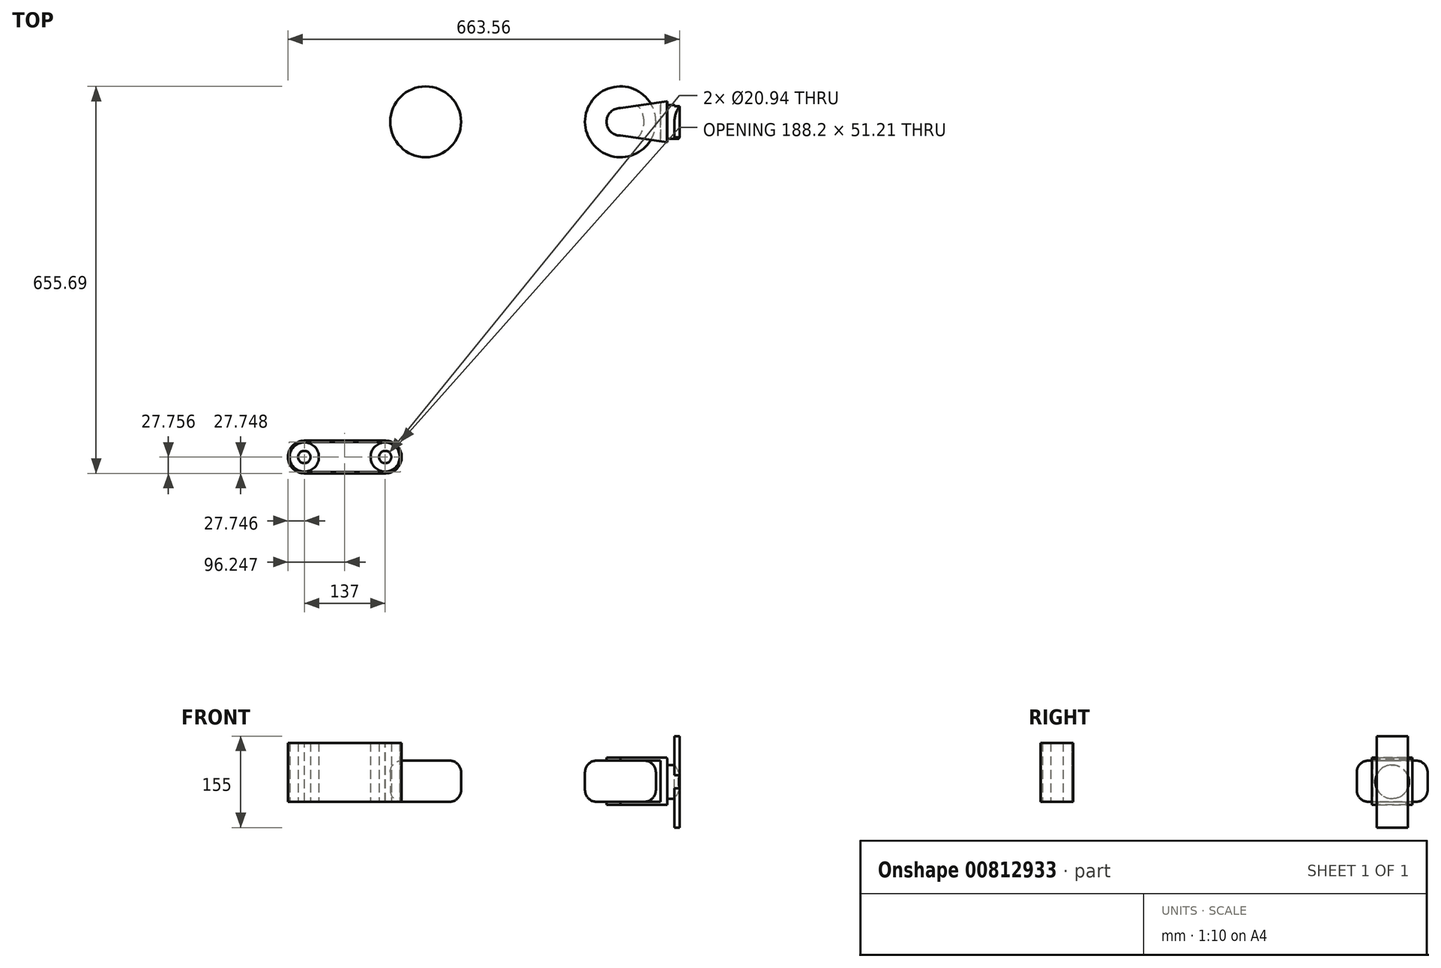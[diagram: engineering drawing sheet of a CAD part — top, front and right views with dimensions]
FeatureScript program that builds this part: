
annotation { "Feature Type Name" : "Feature", "Feature Type Description" : "" }
export const myFeature = defineFeature(function(context is Context, id is Id, definition is map)
    precondition{}
    {
        {
            var Q0;
            Q0=qCreatedBy(makeId("Top.planeOp"),FACE);
            var sketch = newSketch(context, id + "F0", { "sketchPlane" : qUnion([Q0])});
            skCircle(sketch, "E0", {"center": v(-28.53, 29.73) * mm, "radius": 6 * mm});
            skSolve(sketch);
        }
        {
            var Q0;
            Q0=makeQuery(id+"F0.imprint","IMPRINT",FACE,{"disambiguationData":[TD([[makeQuery(id+"F0.imprint","IMPRINT",EDGE,{"derivedFrom":sQuery(id+"F0.wireOp",EDGE,"E0")}),1.0]])]});
            var Q1;
            Q1=sQuery(id+"F0.wireOp",EDGE,"E0");
            extrude(context, id + "F1", {"entities" : qUnion([Q0]), "surfaceEntities" : qUnion([Q1]), "depth" : 7 * mm, "offsetDistance" : 25 * mm});
        }
        {
            var Q0;
            Q0=makeQuery(id+"F1.opExtrude","CAP_EDGE",EDGE,{"disambiguationData":[OSD([sQuery(id+"F0.wireOp",EDGE,"E0")])],"isStart":false});
            var Q1;
            Q1=makeQuery(id+"F1.opExtrude","CAP_EDGE",EDGE,{"disambiguationData":[OSD([sQuery(id+"F0.wireOp",EDGE,"E0")])],"isStart":true});
            fillet(context, id + "F2", {"entities" : qUnion([Q0, Q1]), "radius" : 2 * mm, "tangentPropagation" : true, "allowEdgeOverflow" : false});
        }
        {
            var Q0;
            Q0=makeQuery(id+"F1.opExtrude","SWEPT_BODY",BODY,{"disambiguationData":[OSD([sQuery(id+"F0.wireOp",EDGE,"E0")])]});
            transform(context, id + "F3", {"entities" : qUnion([Q0]), "transformType" : TransformType.TRANSLATION_3D, "dx" : 0 * mm, "dy" : 0 * mm, "dz" : 0 * mm, "makeCopy" : true});
        }
        {
            var Q0;
            Q0=makeQuery(id+"F3.opPattern","COPY",BODY,{"derivedFrom":makeQuery(id+"F1.opExtrude","SWEPT_BODY",BODY,{"disambiguationData":[OSD([sQuery(id+"F0.wireOp",EDGE,"E0")])]}),"instanceName":"1"});
            transform(context, id + "F4", {"entities" : qUnion([Q0]), "transformType" : TransformType.TRANSLATION_3D, "dx" : 33 * mm, "dy" : 0 * mm, "dz" : 0 * mm, "makeCopy" : false});
        }
        {
            var Q0;
            Q0=makeQuery(id+"F3.opPattern","COPY",FACE,{"derivedFrom":makeQuery(id+"F1.opExtrude","CAP_FACE",FACE,{"disambiguationData":[OSD([sQuery(id+"F0.wireOp",EDGE,"E0")])],"isStart":true}),"instanceName":"1"});
            var sketch = newSketch(context, id + "F5", { "sketchPlane" : qUnion([Q0])});
            skCircle(sketch, "E1", {"center": v(4.47, -29.73) * mm, "radius": 2.33 * mm});
            skLineSegment(sketch, "E2", {"start": v(4.47, -27.4) * mm, "end": v(12.39, -26.29) * mm});
            skLineSegment(sketch, "E3", {"start": v(4.47, -32.06) * mm, "end": v(12.39, -33.18) * mm});
            skLineSegment(sketch, "E4", {"start": v(12.39, -33.18) * mm, "end": v(12.39, -26.29) * mm});
            skSolve(sketch);
        }
        {
            var Q0;
            {var subQ0=sQuery(id+"F5.wireOp",EDGE,"E1");var subQ1=makeQuery(id+"F5.imprint","INTERSECT",VERTEX,{"derivedFrom":[subQ0,sQuery(id+"F5.wireOp",EDGE,"E2")]});Q0=makeQuery(id+"F5.imprint","IMPRINT",FACE,{"disambiguationData":[TD([[makeQuery(id+"F5.imprint","IMPRINT",EDGE,{"disambiguationData":[TD([[subQ1,-1.0]])],"derivedFrom":subQ0}),1.0]])]});}
            var Q1;
            {var subQ0=sQuery(id+"F5.wireOp",EDGE,"E2");var subQ1=sQuery(id+"F5.wireOp",EDGE,"E1");var subQ2=makeQuery(id+"F5.imprint","INTERSECT",VERTEX,{"derivedFrom":[subQ1,subQ0]});Q1=makeQuery(id+"F5.imprint","IMPRINT",FACE,{"disambiguationData":[TD([[makeQuery(id+"F5.imprint","IMPRINT",EDGE,{"disambiguationData":[TD([[subQ2,1.0]])],"derivedFrom":subQ1}),-1.0]])]});}
            var Q2;
            {var subQ0=sQuery(id+"F5.wireOp",EDGE,"E4");Q2=makeQuery(id+"F5.imprint","IMPRINT",FACE,{"disambiguationData":[TD([[makeQuery(id+"F5.imprint","IMPRINT",EDGE,{"derivedFrom":subQ0}),1.0]])]});}
            extrude(context, id + "F6", {"entities" : qUnion([Q0, Q1, Q2]), "operationType" : NewBodyOperationType.ADD, "depth" : 0.5 * mm, "offsetDistance" : 25 * mm});
        }
        {
            var Q0;
            Q0=makeQuery(id+"F3.opPattern","COPY",FACE,{"derivedFrom":makeQuery(id+"F1.opExtrude","CAP_FACE",FACE,{"disambiguationData":[OSD([sQuery(id+"F0.wireOp",EDGE,"E0")])],"isStart":false}),"instanceName":"1"});
            var sketch = newSketch(context, id + "F7", { "sketchPlane" : qUnion([Q0])});
            skCircle(sketch, "E5", {"center": v(4.44, 29.73) * mm, "radius": 2.33 * mm});
            skLineSegment(sketch, "E6", {"start": v(4.44, 32.06) * mm, "end": v(12.36, 33.18) * mm});
            skLineSegment(sketch, "E7", {"start": v(4.44, 27.4) * mm, "end": v(12.36, 26.29) * mm});
            skLineSegment(sketch, "E8", {"start": v(12.36, 26.29) * mm, "end": v(12.36, 33.18) * mm});
            skSolve(sketch);
        }
        {
            var Q0;
            Q0 = qSketchRegion(id + "F7", true);
            extrude(context, id + "F8", {"entities" : qUnion([Q0]), "operationType" : NewBodyOperationType.ADD, "depth" : 0.5 * mm, "offsetDistance" : 25 * mm});
        }
        {
            var Q0;
            Q0=makeQuery(id+"F6.opExtrude","CAP_FACE",FACE,{"disambiguationData":[OSD([sQuery(id+"F5.wireOp",EDGE,"E1"),sQuery(id+"F5.wireOp",EDGE,"E2"),sQuery(id+"F5.wireOp",EDGE,"E3"),sQuery(id+"F5.wireOp",EDGE,"E4")])],"isStart":true});
            var sketch = newSketch(context, id + "F9", { "sketchPlane" : qUnion([Q0])});
            skLineSegment(sketch, "E9", {"start": v(11.26, 33.02) * mm, "end": v(12.39, 33.18) * mm});
            skLineSegment(sketch, "E10", {"start": v(12.39, 33.18) * mm, "end": v(12.39, 26.29) * mm});
            skLineSegment(sketch, "E11", {"start": v(12.39, 26.29) * mm, "end": v(11.26, 26.44) * mm});
            skLineSegment(sketch, "E12", {"start": v(11.26, 26.44) * mm, "end": v(11.26, 33.02) * mm});
            skSolve(sketch);
        }
        {
            var Q0;
            Q0 = qSketchRegion(id + "F9", true);
            extrude(context, id + "F10", {"entities" : qUnion([Q0]), "operationType" : NewBodyOperationType.ADD, "depth" : 7.3 * mm, "offsetDistance" : 25 * mm});
        }
        {
            var Q0;
            Q0=makeQuery(id+"F10.boolean.opBoolean","MERGE",FACE,{"derivedFrom":[makeQuery(id+"F6.opExtrude","SWEPT_FACE",FACE,{"disambiguationData":[OSD([sQuery(id+"F5.wireOp",EDGE,"E4")])]}),makeQuery(id+"F10.opExtrude","SWEPT_FACE",FACE,{"disambiguationData":[OSD([sQuery(id+"F9.wireOp",EDGE,"E10")])]})]});
            var sketch = newSketch(context, id + "F11", { "sketchPlane" : qUnion([Q0])});
            skCircle(sketch, "E13", {"center": v(29.73, 3.4) * mm, "radius": 2.86 * mm});
            skPoint(sketch, "E13.centerSnap0", {"position": v(26.29, 3.4) * mm});
            skPoint(sketch, "E13.centerSnap1", {"position": v(29.73, 7.3) * mm});
            skSolve(sketch);
        }
        {
            var Q0;
            Q0 = qSketchRegion(id + "F11", true);
            extrude(context, id + "F12", {"entities" : qUnion([Q0]), "operationType" : NewBodyOperationType.ADD, "depth" : 1.2 * mm, "offsetDistance" : 25 * mm});
        }
        {
            var Q0;
            Q0=makeQuery(id+"F12.opExtrude","CAP_FACE",FACE,{"disambiguationData":[OSD([sQuery(id+"F11.wireOp",EDGE,"E13")])],"isStart":false});
            var sketch = newSketch(context, id + "F13", { "sketchPlane" : qUnion([Q0])});
            skLineSegment(sketch, "E14.bottom", {"start": v(32.37, -4.35) * mm, "end": v(27.1, -4.35) * mm});
            skLineSegment(sketch, "E14.top", {"start": v(32.37, 11.15) * mm, "end": v(27.1, 11.15) * mm});
            skLineSegment(sketch, "E14.left", {"start": v(32.37, -4.35) * mm, "end": v(32.37, 11.15) * mm});
            skLineSegment(sketch, "E14.right", {"start": v(27.1, -4.35) * mm, "end": v(27.1, 11.15) * mm});
            skPoint(sketch, "E14.middle", {"position": v(29.73, 3.4) * mm});
            skSolve(sketch);
        }
        {
            var Q0;
            {var subQ0=sQuery(id+"F13.wireOp",EDGE,"E14.top");Q0=makeQuery(id+"F13.imprint","IMPRINT",FACE,{"disambiguationData":[TD([[makeQuery(id+"F13.imprint","IMPRINT",EDGE,{"derivedFrom":subQ0}),1.0]])]});}
            var Q1;
            {var subQ0=sQuery(id+"F13.wireOp",EDGE,"E14.bottom");Q1=makeQuery(id+"F13.imprint","IMPRINT",FACE,{"disambiguationData":[TD([[makeQuery(id+"F13.imprint","IMPRINT",EDGE,{"derivedFrom":subQ0}),-1.0]])]});}
            var Q2;
            {var subQ0=sQuery(id+"F13.wireOp",EDGE,"E14.left");var subQ1=makeQuery(id+"F12.opExtrude","CAP_EDGE",EDGE,{"disambiguationData":[OSD([sQuery(id+"F11.wireOp",EDGE,"E13")])],"isStart":false});var subQ2=makeQuery(id+"F13.imprint","INTERSECT",VERTEX,{"disambiguationData":[OD(0.0)],"derivedFrom":[subQ1,subQ0]});Q2=makeQuery(id+"F13.imprint","IMPRINT",FACE,{"disambiguationData":[TD([[makeQuery(id+"F13.imprint","IMPRINT",EDGE,{"disambiguationData":[TD([[subQ2,-1.0]])],"derivedFrom":subQ0}),1.0]])]});}
            extrude(context, id + "F14", {"entities" : qUnion([Q0, Q1, Q2]), "operationType" : NewBodyOperationType.ADD, "depth" : 0.9 * mm, "offsetDistance" : 25 * mm});
        }
        {
            var Q0;
            {var subQ0=sQuery(id+"F13.wireOp",EDGE,"E14.left");Q0=makeQuery(id+"F14.boolean.opBoolean","SPLIT",EDGE,{"disambiguationData":[topologyDisambiguationEdgeConnected([makeQuery(id+"F12.opExtrude","CAP_FACE",FACE,{"disambiguationData":[OSD([sQuery(id+"F11.wireOp",EDGE,"E13")])],"isStart":false}),makeQuery(id+"F14.opExtrude","SWEPT_FACE",FACE,{"disambiguationData":[OSD([subQ0])]})])],"derivedFrom":makeQuery(id+"F14.opExtrude","CAP_EDGE",EDGE,{"disambiguationData":[OSD([subQ0])],"isStart":true})});}
            fillet(context, id + "F15", {"entities" : qUnion([Q0]), "radius" : 5 * mm, "tangentPropagation" : true, "allowEdgeOverflow" : false});
        }
        {
            var Q0;
            {var subQ0=sQuery(id+"F13.wireOp",EDGE,"E14.right");Q0=makeQuery(id+"F14.boolean.opBoolean","SPLIT",EDGE,{"disambiguationData":[topologyDisambiguationEdgeConnected([makeQuery(id+"F12.opExtrude","CAP_FACE",FACE,{"disambiguationData":[OSD([sQuery(id+"F11.wireOp",EDGE,"E13")])],"isStart":false}),makeQuery(id+"F14.opExtrude","SWEPT_FACE",FACE,{"disambiguationData":[OSD([subQ0])]})])],"derivedFrom":makeQuery(id+"F14.opExtrude","CAP_EDGE",EDGE,{"disambiguationData":[OSD([subQ0])],"isStart":true})});}
            fillet(context, id + "F16", {"entities" : qUnion([Q0]), "radius" : 5 * mm, "tangentPropagation" : true, "allowEdgeOverflow" : false});
        }
        {
            var Q0;
            Q0=qCreatedBy(makeId("Top.planeOp"),FACE);
            var sketch = newSketch(context, id + "F17", { "sketchPlane" : qUnion([Q0])});
            skCircle(sketch, "E15", {"center": v(-49.1, -27.06) * mm, "radius": 2.47 * mm});
            skCircle(sketch, "E16", {"center": v(-49.1, -27.06) * mm, "radius": 1.05 * mm});
            skSolve(sketch);
        }
        {
            var Q0;
            Q0=makeQuery(id+"F17.imprint","IMPRINT",FACE,{"disambiguationData":[TD([[makeQuery(id+"F17.imprint","IMPRINT",EDGE,{"derivedFrom":sQuery(id+"F17.wireOp",EDGE,"E15")}),1.0]])]});
            extrude(context, id + "F18", {"entities" : qUnion([Q0]), "depth" : 10 * mm, "offsetDistance" : 25 * mm});
        }
        {
            var Q0;
            Q0=makeQuery(id+"F18.opExtrude","SWEPT_BODY",BODY,{"disambiguationData":[OSD([sQuery(id+"F17.wireOp",EDGE,"E15"),sQuery(id+"F17.wireOp",EDGE,"E16")])]});
            transform(context, id + "F19", {"entities" : qUnion([Q0]), "transformType" : TransformType.TRANSLATION_3D, "dx" : 13.7 * mm, "dy" : 0 * mm, "dz" : 0 * mm, "makeCopy" : true});
        }
        {
            var Q0;
            Q0=makeQuery(id+"F18.opExtrude","CAP_FACE",FACE,{"disambiguationData":[OSD([sQuery(id+"F17.wireOp",EDGE,"E15"),sQuery(id+"F17.wireOp",EDGE,"E16")])],"isStart":false});
            var sketch = newSketch(context, id + "F20", { "sketchPlane" : qUnion([Q0])});
            skCircle(sketch, "E17", {"center": v(-49.1, -27.06) * mm, "radius": 2.56 * mm});
            skCircle(sketch, "E18", {"center": v(-35.4, -27.06) * mm, "radius": 2.56 * mm});
            skLineSegment(sketch, "E19.bottom", {"start": v(-49.1, -27.06) * mm, "end": v(-35.36, -27.06) * mm});
            skLineSegment(sketch, "E19.top", {"start": v(-49.1, -24.5) * mm, "end": v(-35.36, -24.5) * mm});
            skLineSegment(sketch, "E19.left", {"start": v(-49.1, -27.06) * mm, "end": v(-49.1, -24.5) * mm});
            skLineSegment(sketch, "E19.right", {"start": v(-35.36, -27.06) * mm, "end": v(-35.36, -24.5) * mm});
            skLineSegment(sketch, "E20.bottom", {"start": v(-35.36, -27.06) * mm, "end": v(-49.1, -27.06) * mm});
            skLineSegment(sketch, "E20.top", {"start": v(-35.36, -29.62) * mm, "end": v(-49.1, -29.62) * mm});
            skLineSegment(sketch, "E20.left", {"start": v(-35.36, -27.06) * mm, "end": v(-35.36, -29.62) * mm});
            skLineSegment(sketch, "E20.right", {"start": v(-49.1, -27.06) * mm, "end": v(-49.1, -29.62) * mm});
            skCircle(sketch, "E21", {"center": v(-49.1, -27.06) * mm, "radius": 2.77 * mm});
            skCircle(sketch, "E22", {"center": v(-35.36, -27.06) * mm, "radius": 2.77 * mm});
            skLineSegment(sketch, "E23", {"start": v(-49.1, -24.29) * mm, "end": v(-35.36, -24.29) * mm});
            skLineSegment(sketch, "E24", {"start": v(-35.36, -24.29) * mm, "end": v(-35.36, -29.84) * mm});
            skLineSegment(sketch, "E25", {"start": v(-35.36, -29.84) * mm, "end": v(-49.1, -29.84) * mm});
            skSolve(sketch);
        }
        {
            var Q0;
            {var subQ5=sQuery(id+"F20.wireOp",EDGE,"E19.left");var subQ7=sQuery(id+"F20.wireOp",EDGE,"E19.top");var subQ8=makeQuery(id+"F20.imprint","INTERSECT",VERTEX,{"derivedFrom":[subQ7,subQ5]});Q0=makeQuery(id+"F20.imprint","IMPRINT",FACE,{"disambiguationData":[TD([[makeQuery(id+"F20.imprint","IMPRINT",EDGE,{"disambiguationData":[TD([[subQ8,-1.0]])],"derivedFrom":subQ7}),1.0]])]});}
            var Q1;
            {var subQ5=sQuery(id+"F20.wireOp",EDGE,"E23");Q1=makeQuery(id+"F20.imprint","IMPRINT",FACE,{"disambiguationData":[TD([[makeQuery(id+"F20.imprint","IMPRINT",EDGE,{"derivedFrom":subQ5}),-1.0]])]});}
            var Q2;
            {var subQ0=sQuery(id+"F20.wireOp",EDGE,"E24");var subQ3=sQuery(id+"F20.wireOp",EDGE,"E18");var subQ4=makeQuery(id+"F20.imprint","INTERSECT",VERTEX,{"disambiguationData":[OD(0.0)],"derivedFrom":[subQ3,subQ0]});Q2=makeQuery(id+"F20.imprint","IMPRINT",FACE,{"disambiguationData":[TD([[makeQuery(id+"F20.imprint","IMPRINT",EDGE,{"disambiguationData":[TD([[subQ4,1.0]])],"derivedFrom":subQ3}),-1.0]])]});}
            var Q3;
            {var subQ5=sQuery(id+"F20.wireOp",EDGE,"E25");Q3=makeQuery(id+"F20.imprint","IMPRINT",FACE,{"disambiguationData":[TD([[makeQuery(id+"F20.imprint","IMPRINT",EDGE,{"derivedFrom":subQ5}),-1.0]])]});}
            var Q4;
            {var subQ0=sQuery(id+"F20.wireOp",EDGE,"E24");var subQ1=sQuery(id+"F20.wireOp",EDGE,"E20.top");var subQ2=makeQuery(id+"F20.imprint","INTERSECT",VERTEX,{"derivedFrom":[subQ1,subQ0]});Q4=makeQuery(id+"F20.imprint","IMPRINT",FACE,{"disambiguationData":[TD([[makeQuery(id+"F20.imprint","IMPRINT",EDGE,{"disambiguationData":[TD([[subQ2,-1.0]])],"derivedFrom":subQ1}),1.0]])]});}
            var Q5;
            {var subQ0=sQuery(id+"F20.wireOp",EDGE,"E19.top");var subQ1=sQuery(id+"F20.wireOp",EDGE,"E18");var subQ2=makeQuery(id+"F20.imprint","INTERSECT",VERTEX,{"derivedFrom":[subQ1,subQ0]});Q5=makeQuery(id+"F20.imprint","IMPRINT",FACE,{"disambiguationData":[TD([[makeQuery(id+"F20.imprint","IMPRINT",EDGE,{"disambiguationData":[TD([[subQ2,1.0]])],"derivedFrom":subQ1}),-1.0]])]});}
            extrude(context, id + "F21", {"entities" : qUnion([Q0, Q1, Q2, Q3, Q4, Q5]), "oppositeDirection" : true, "depth" : 10 * mm, "offsetDistance" : 25 * mm});
        }
        {
            var Q0;
            Q0=makeQuery(id+"F1.opExtrude","SWEPT_BODY",BODY,{"disambiguationData":[OSD([sQuery(id+"F0.wireOp",EDGE,"E0")])]});
            var Q1;
            Q1=makeQuery(id+"F3.opPattern","COPY",BODY,{"derivedFrom":makeQuery(id+"F1.opExtrude","SWEPT_BODY",BODY,{"disambiguationData":[OSD([sQuery(id+"F0.wireOp",EDGE,"E0")])]}),"instanceName":"1"});
            var Q2;
            Q2=makeQuery(id+"F18.opExtrude","SWEPT_BODY",BODY,{"disambiguationData":[OSD([sQuery(id+"F17.wireOp",EDGE,"E15"),sQuery(id+"F17.wireOp",EDGE,"E16")])]});
            var Q3;
            Q3=makeQuery(id+"F19.opPattern","COPY",BODY,{"derivedFrom":makeQuery(id+"F18.opExtrude","SWEPT_BODY",BODY,{"disambiguationData":[OSD([sQuery(id+"F17.wireOp",EDGE,"E15"),sQuery(id+"F17.wireOp",EDGE,"E16")])]}),"instanceName":"1"});
            var Q4;
            Q4=makeQuery(id+"F21.opExtrude","SWEPT_BODY",BODY,{"disambiguationData":[OSD([sQuery(id+"F20.wireOp",EDGE,"E17"),sQuery(id+"F20.wireOp",EDGE,"E18"),sQuery(id+"F20.wireOp",EDGE,"E19.top"),sQuery(id+"F20.wireOp",EDGE,"E19.left"),sQuery(id+"F20.wireOp",EDGE,"E20.top"),sQuery(id+"F20.wireOp",EDGE,"E21"),sQuery(id+"F20.wireOp",EDGE,"E22"),sQuery(id+"F20.wireOp",EDGE,"E23"),sQuery(id+"F20.wireOp",EDGE,"E24"),sQuery(id+"F20.wireOp",EDGE,"E25")])]});
            var Q5;
            Q5=makeQuery(id+"F21.opExtrude","CAP_VERTEX",VERTEX,{"disambiguationData":[OSD([sQuery(id+"F20.wireOp",EDGE,"E21"),sQuery(id+"F20.wireOp",EDGE,"E25")])],"isStart":false});
            transform(context, id + "F22", {"entities" : qUnion([Q0, Q1, Q2, Q3, Q4]), "transformType" : TransformType.SCALE_UNIFORMLY, "scale" : 10, "scalePoint" : qUnion([Q5]), "makeCopy" : false});
        }
    });
